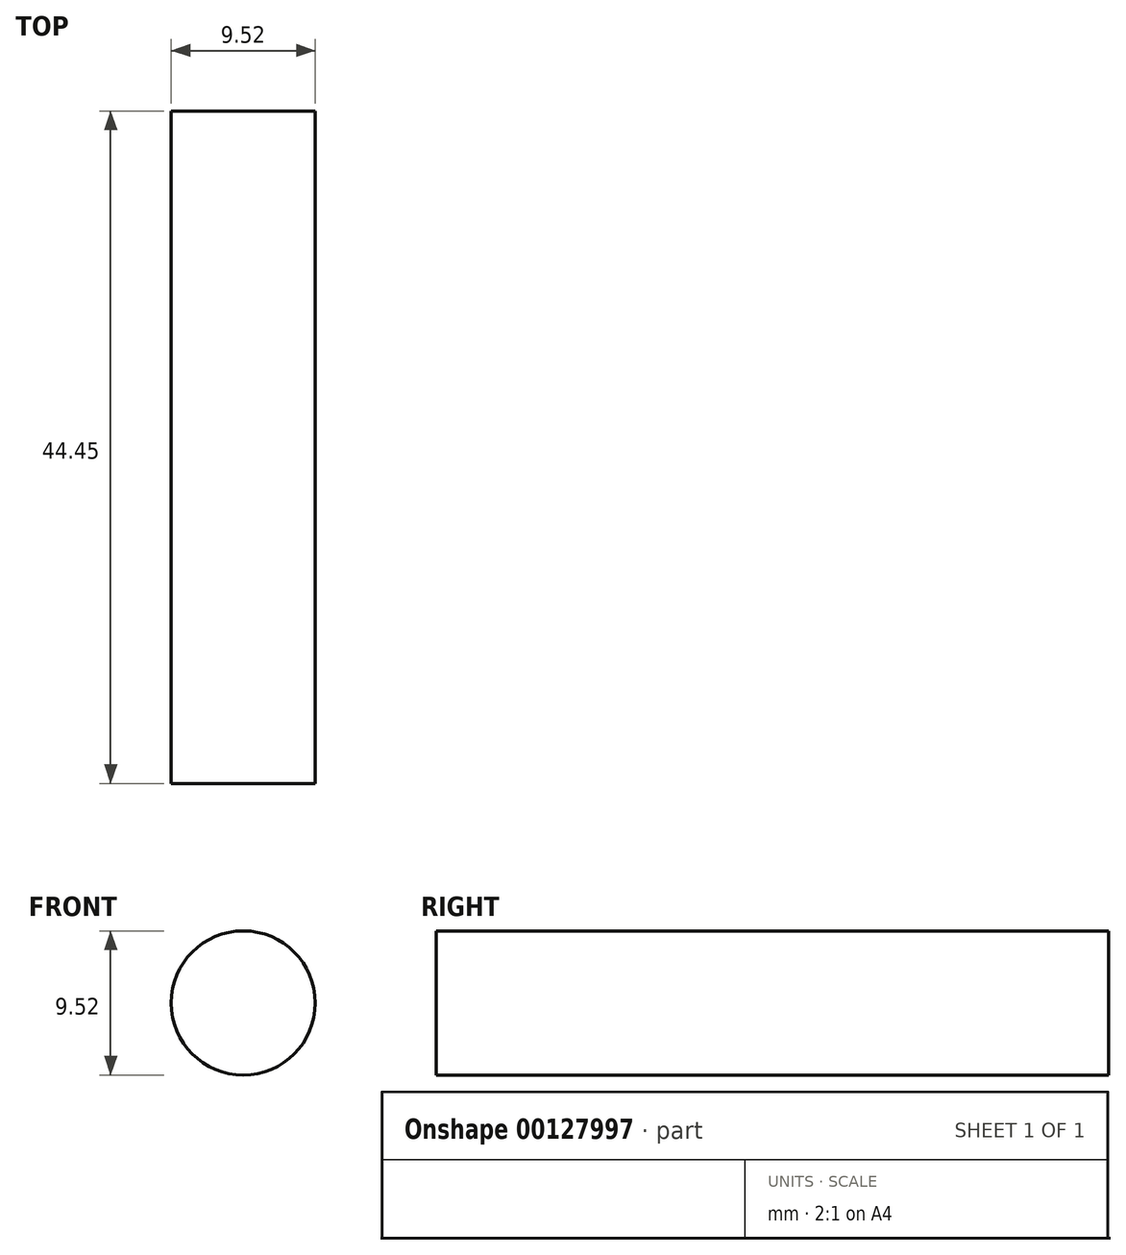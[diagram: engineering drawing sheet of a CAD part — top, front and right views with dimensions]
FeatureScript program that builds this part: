
annotation { "Feature Type Name" : "Feature", "Feature Type Description" : "" }
export const myFeature = defineFeature(function(context is Context, id is Id, definition is map)
    precondition{}
    {
        {
            var Q0;
            Q0=qCreatedBy(makeId("Front.planeOp"),FACE);
            var sketch = newSketch(context, id + "F0", { "sketchPlane" : qUnion([Q0])});
            skCircle(sketch, "E0", {"center": v(0, 0) * mm, "radius": 4.76 * mm});
            skSolve(sketch);
        }
        {
            var Q0;
            Q0 = qSketchRegion(id + "F0", true);
            extrude(context, id + "F1", {"entities" : qUnion([Q0]), "depth" : 44.45 * mm});
        }
    });
